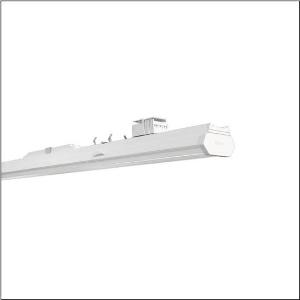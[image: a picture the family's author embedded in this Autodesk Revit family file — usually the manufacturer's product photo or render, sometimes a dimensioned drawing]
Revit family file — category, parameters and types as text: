
# Revit family: licross_r__11_protected_mo_51tp127n58xf_03c6
name_source: partatom
category: Lighting Fixtures
units: mm (PartAtom-declared; Revit-internal decimal feet)

## family parameters
Cut with Voids When Loaded = No
Host = Face
Light Source = No
Part Type = Normal
Room Calculation Point = No
Round Connector Dimension = Use Diameter
Shared = No

## types (1)
- Licross® 11 Protected MO (1 x LED, 8120 lm, 47.6 W, 5000K)
    Apparent Load = 48 VA
    CIE Flux Codes = 73 92 98 99 100
    Color Rendering = 80
    Color Temperature = 5000K
    Default Elevation = 1800 mm
    Description = Licross® 11 Protected MO, luminaire insert, of sheet steel, galvanised, coil coated, white, length: 1.500mm, width: 90mm, height: 101mm, LED rated luminous flux: 8.120lm, light colour: 850, control gear: ON/OFF, control gear: ECG, with plug, 3-pole, with phase selection, mains connection: 220..240V, AC, 50/60Hz, rated input power: 48W, halogen-free wiring, primary optical cover: cover, of PMMA, light emission: direct distribution, primary light characteristic: symmetric, protection rating (complete): IP64, insulation class (complete): insulation class I (protective earthing), certification: CE, ENEC, VDE, UKCA, protection symbol: D if used in an environment with conductive dust loads with corresponding accessories, impact resistance: IK06, permissible ambient temperature for indoor applications: -35..+45°C, reducing of maximum allowable ambient temperature of 5°C with ceiling mounting, corresponds to IFS (International Featured Standards) requirements for safety and quality in the food industry, LABS conformity tested according to VDMA 24364:2018-05, packaging unit: 1 piece
    Height = 92 mm
    Lamp = 1 x LED
    Lamp Light Flux = 8120 lm
    Lamp Power = 47.6 W
    Lamp count = 1
    Length = 1500 mm
    Luminous efficacy = 171 lm/W
    Manufacturer = Siteco
    ModVariant = No
    Model = 51TP127N58XF
    Mounting Place = Ceiling
    Mounting Type = Pendant
    Number of Poles = 1
    OnlyDefault = Yes
    Power Factor = 1
    Product Name = Licross® 11 Protected MO
    Product group = luminaire insert
    ProductGroupID = 901
    Protection Class = Protection class I
    Protection Degree = IP 64
    RLX_Detail_Level = 1
    RLX_Emergency_Light_Flux = 0 lm
    RLX_Emergency_Type = 0
    RLX_Emergency_Type_DB = No
    RlxData = <blob elided: 20625 chars, md5=928ff1c4>
    Socket = socket
    Standby Power = 0 W
    System Light Flux = 8120 lm
    System Power = 48 W
    Type Comments = Product without accessories
    Type Image = l_1256148.jpg
    URL = http://relux.com
    VarID = ---
    Voltage = 0 V
    Weight = 0.00 kg
    Width = 88 mm

## geometry (parser evidence)
native form markers: Blend x4, Sweep x11
no freeform markers — native parametric forms only
